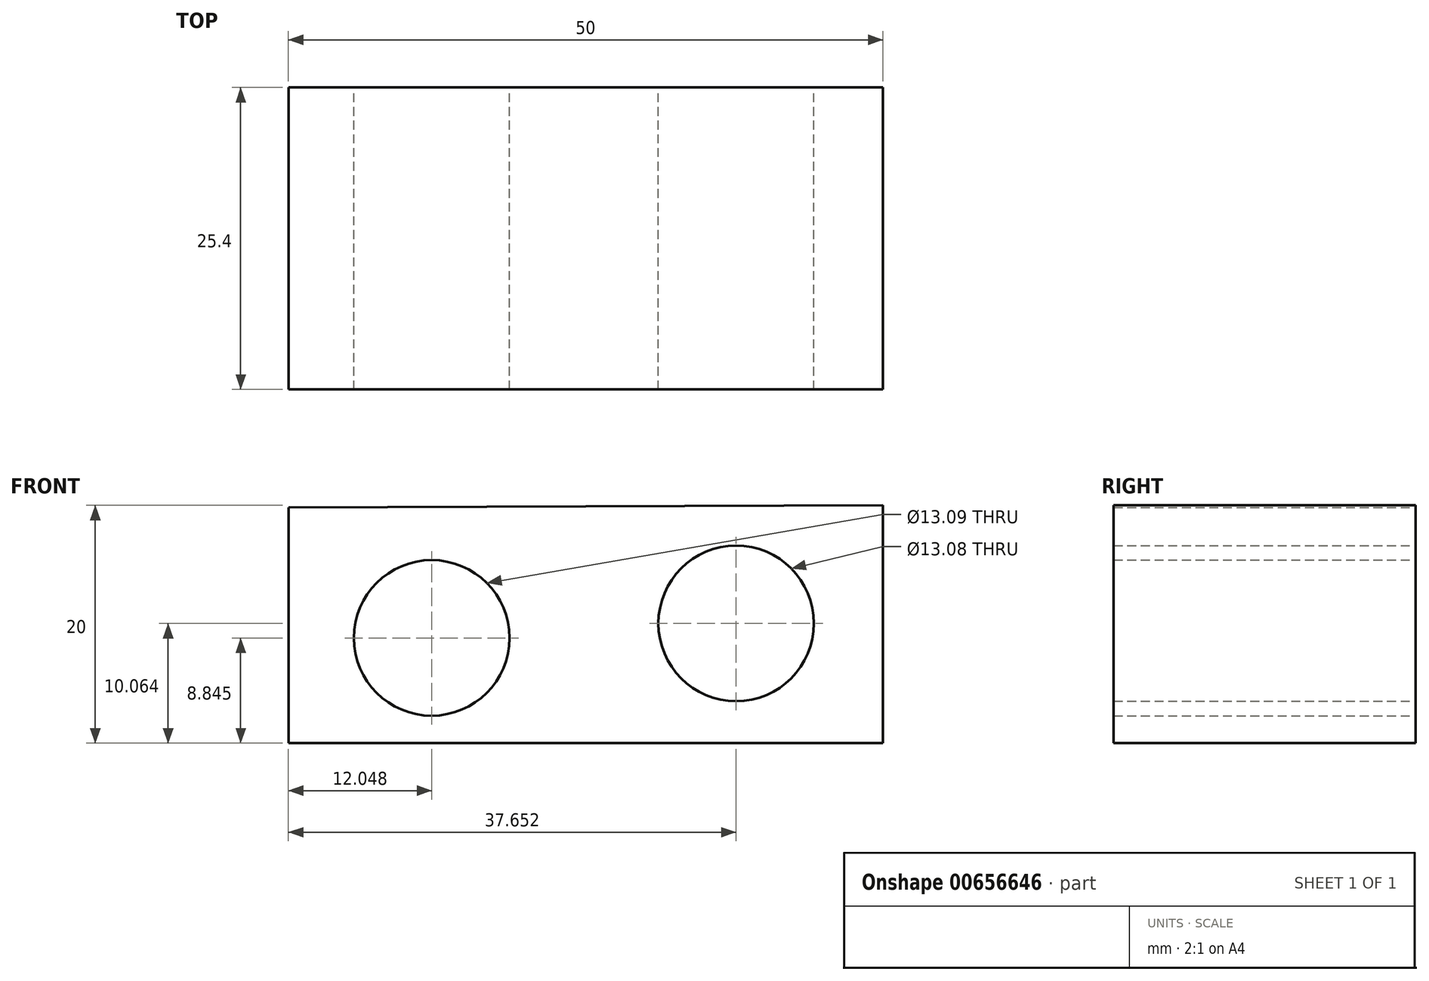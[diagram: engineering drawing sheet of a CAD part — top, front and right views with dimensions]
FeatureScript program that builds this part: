
annotation { "Feature Type Name" : "Feature", "Feature Type Description" : "" }
export const myFeature = defineFeature(function(context is Context, id is Id, definition is map)
    precondition{}
    {
        {
            var Q0;
            Q0=qCreatedBy(makeId("Front.planeOp"),FACE);
            var sketch = newSketch(context, id + "F0", { "sketchPlane" : qUnion([Q0])});
            skLineSegment(sketch, "E0", {"start": v(-21.04, 3.03) * mm, "end": v(-21.04, -16.77) * mm});
            skLineSegment(sketch, "E1", {"start": v(-21.04, -16.77) * mm, "end": v(28.96, -16.77) * mm});
            skLineSegment(sketch, "E2", {"start": v(28.96, -16.77) * mm, "end": v(28.96, 3.23) * mm});
            skLineSegment(sketch, "E3", {"start": v(28.96, 3.23) * mm, "end": v(-21.04, 3.03) * mm});
            skCircle(sketch, "E4", {"center": v(-9, -7.92) * mm, "radius": 6.54 * mm});
            skCircle(sketch, "E5", {"center": v(16.61, -6.7) * mm, "radius": 6.54 * mm});
            skSolve(sketch);
        }
        {
            var Q0;
            Q0 = qSketchRegion(id + "F0", true);
            extrude(context, id + "F1", {"entities" : qUnion([Q0]), "depth" : 25.4 * mm, "offsetDistance" : 25.4 * mm});
        }
        {
            var Q0;
            Q0 = qSketchRegion(id + "F0", true);
            extrude(context, id + "F2", {"entities" : qUnion([Q0]), "operationType" : NewBodyOperationType.ADD, "depth" : 25.4 * mm, "offsetDistance" : 25.4 * mm});
        }
    });
